# Revit family: Конвектор WSK-141 подключение справа
name_source: partatom
category: Оборудование
revit_build: Autodesk Revit 2017 (Build: 20181011_1545(x64)
units: mm (PartAtom-declared; Revit-internal decimal feet)

## family parameters
Всегда вертикально = Да
На основе рабочей плоскости = Нет
Общий = Нет
При загрузке вырезать с полостями = Нет
Размер круглого соединителя = Использовать диаметр
Тип детали = Нормальный
Точка расчета площади = Нет

## types (4) — shared parameters
ADSK_Завод-изготовитель = Moehlenhoff
D = 15 мм
ID01 = Стандартное
ID02 = Сбоку
ID03 = Снизу
KA = 23 мм
KB1 = 34 мм
KB2 = 50 мм
KB3 = 50 мм
MA1 = 20 мм
MA2 = 33 мм
MA3 = 33 мм
MD = 30 мм
MH = 47 мм
t01 = t01
t03 = t03
t04 = t04_r
t05 = t05_r
tcode = tcode_r
Высота = 141 мм
Изготовитель = Moehlenhoff
Корпус = <По категории>
Разработчик = ООО ПРОРУБИМ
Разработчик (URL) = http://prorubim.com
Разработчик (телефон) = +7(495)649-85-43
Решетка толщина = 15 мм

## per-type parameters (varying)
| type | Решетка ширина | Ширина |
| WSK-180x141h | 174 мм | 180 мм |
| WSK-260x141h | 254 мм | 260 мм |
| WSK-320x141h | 314 мм | 320 мм |
| WSK-410x141h | 314 мм | 320 мм |
